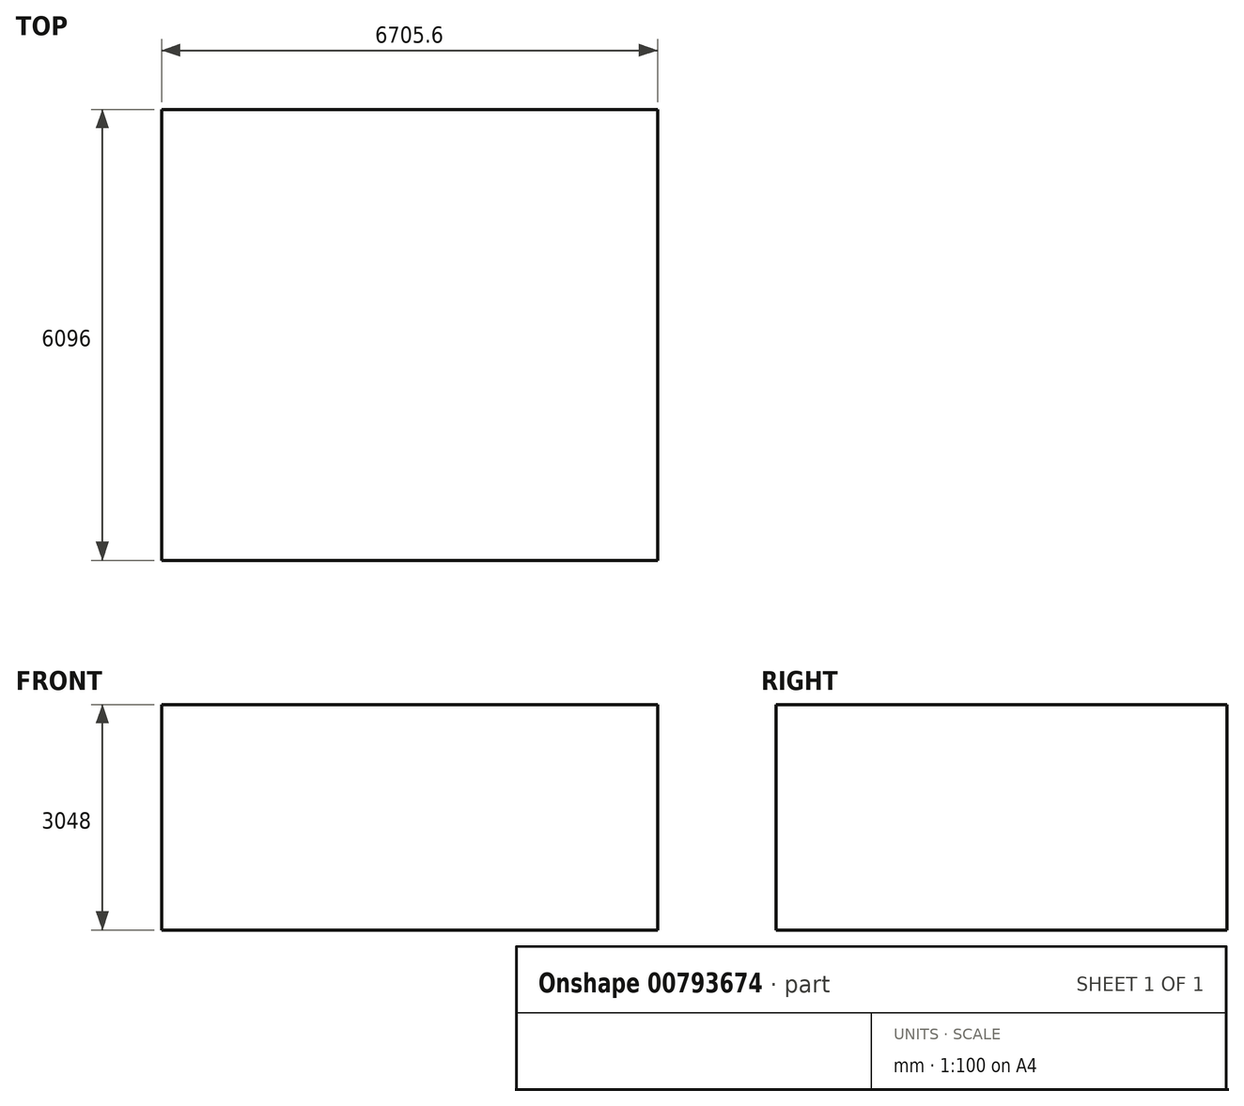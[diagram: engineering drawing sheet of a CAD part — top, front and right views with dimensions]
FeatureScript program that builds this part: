
annotation { "Feature Type Name" : "Feature", "Feature Type Description" : "" }
export const myFeature = defineFeature(function(context is Context, id is Id, definition is map)
    precondition{}
    {
        {
            var Q0;
            Q0=qCreatedBy(makeId("Top.planeOp"),FACE);
            var sketch = newSketch(context, id + "F0", { "sketchPlane" : qUnion([Q0])});
            skLineSegment(sketch, "E0.bottom", {"start": v(-3351.2, -2178.64) * mm, "end": v(3354.4, -2178.64) * mm});
            skLineSegment(sketch, "E0.top", {"start": v(-3351.2, 3917.36) * mm, "end": v(3354.4, 3917.36) * mm});
            skLineSegment(sketch, "E0.left", {"start": v(-3351.2, -2178.64) * mm, "end": v(-3351.2, 3917.36) * mm});
            skLineSegment(sketch, "E0.right", {"start": v(3354.4, -2178.64) * mm, "end": v(3354.4, 3917.36) * mm});
            skSolve(sketch);
        }
        {
            var Q0;
            Q0 = qSketchRegion(id + "F0", true);
            extrude(context, id + "F1", {"entities" : qUnion([Q0]), "depth" : 3048 * mm, "offsetDistance" : 25.4 * mm});
        }
    });
